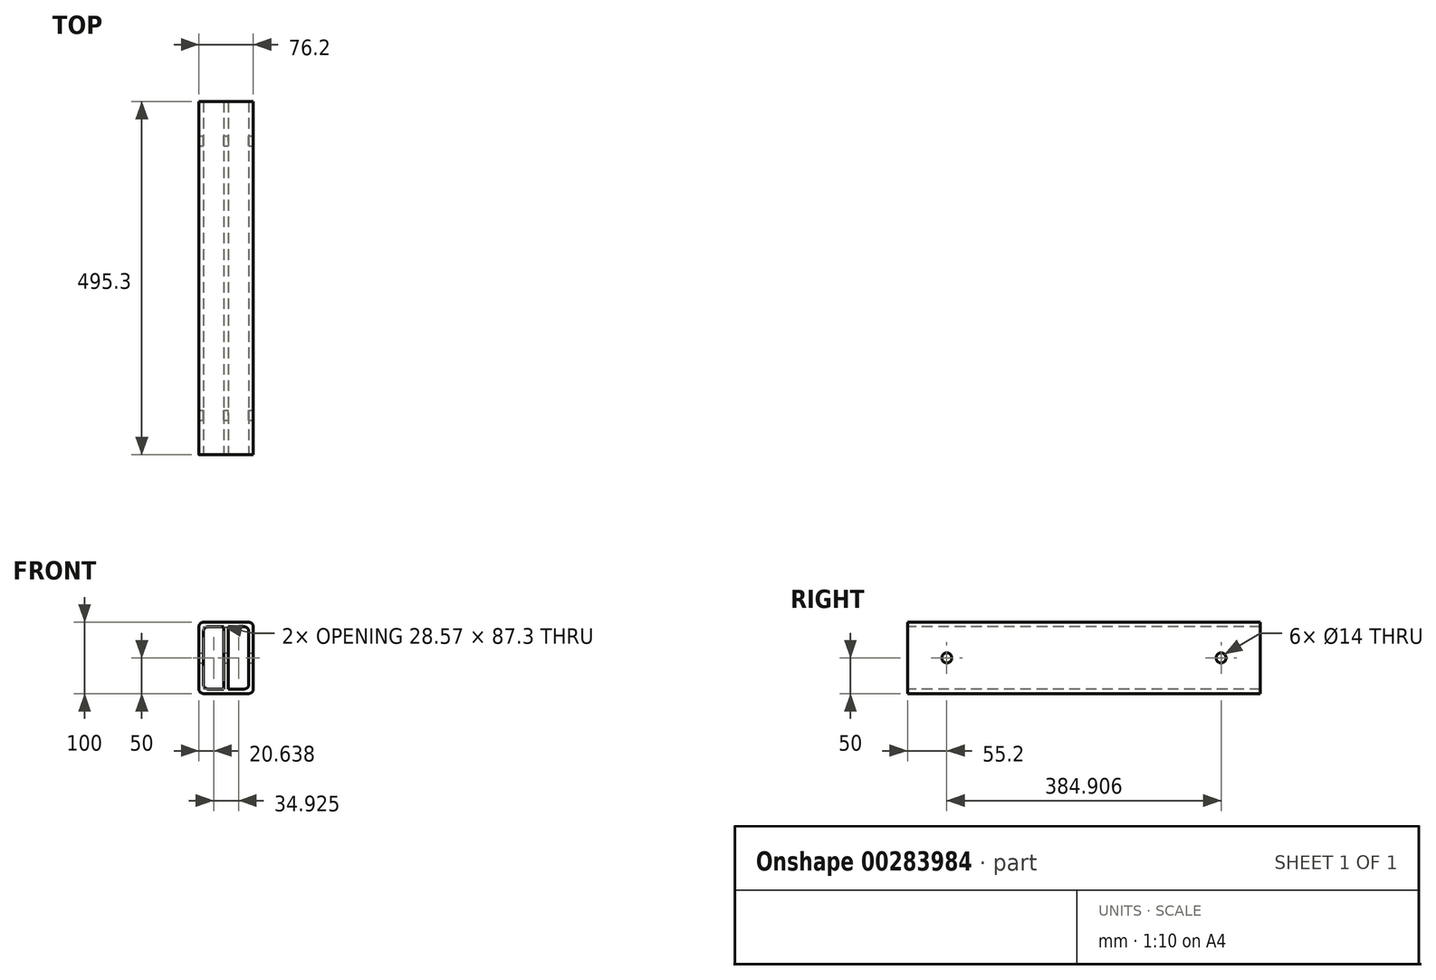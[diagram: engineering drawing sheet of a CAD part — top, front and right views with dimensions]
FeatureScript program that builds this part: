
annotation { "Feature Type Name" : "Feature", "Feature Type Description" : "" }
export const myFeature = defineFeature(function(context is Context, id is Id, definition is map)
    precondition{}
    {
        {
            var Q0;
            Q0=qCreatedBy(makeId("Front.planeOp"),FACE);
            var sketch = newSketch(context, id + "F0", { "sketchPlane" : qUnion([Q0])});
            skLineSegment(sketch, "E0.bottom", {"start": v(31.75, -50) * mm, "end": v(-31.75, -50) * mm});
            skLineSegment(sketch, "E0.top", {"start": v(31.75, 50) * mm, "end": v(-31.75, 50) * mm});
            skLineSegment(sketch, "E0.left", {"start": v(38.1, -43.65) * mm, "end": v(38.1, 43.65) * mm});
            skLineSegment(sketch, "E0.right", {"start": v(-38.1, -43.65) * mm, "end": v(-38.1, 43.65) * mm});
            skPoint(sketch, "E0.middle", {"position": v(0, 0) * mm});
            skLineSegment(sketch, "E1.bottom", {"start": v(25.4, -43.65) * mm, "end": v(-25.4, -43.65) * mm});
            skLineSegment(sketch, "E1.top", {"start": v(25.4, 43.65) * mm, "end": v(-25.4, 43.65) * mm});
            skLineSegment(sketch, "E1.left", {"start": v(31.75, -37.3) * mm, "end": v(31.75, 37.3) * mm});
            skLineSegment(sketch, "E1.right", {"start": v(-31.75, -37.3) * mm, "end": v(-31.75, 37.3) * mm});
            skPoint(sketch, "E2.visualSharp", {"position": v(-38.1, 50) * mm});
            skArc(sketch, "E2.filletArc", {"start": v(-31.75, 50) * mm, "mid": v(-36.24, 48.14) * mm, "end": v(-38.1, 43.65) * mm});
            skArc(sketch, "E3.filletArc", {"start": v(-25.4, 43.65) * mm, "mid": v(-29.9, 41.8) * mm, "end": v(-31.75, 37.3) * mm});
            skPoint(sketch, "E4.visualSharp", {"position": v(31.75, 43.65) * mm});
            skArc(sketch, "E4.filletArc", {"start": v(31.75, 37.3) * mm, "mid": v(29.9, 41.8) * mm, "end": v(25.4, 43.65) * mm});
            skPoint(sketch, "E5.visualSharp", {"position": v(38.1, 50) * mm});
            skArc(sketch, "E5.filletArc", {"start": v(38.1, 43.65) * mm, "mid": v(36.24, 48.14) * mm, "end": v(31.75, 50) * mm});
            skPoint(sketch, "E6.visualSharp", {"position": v(31.75, -43.65) * mm});
            skArc(sketch, "E6.filletArc", {"start": v(25.4, -43.65) * mm, "mid": v(29.9, -41.8) * mm, "end": v(31.75, -37.3) * mm});
            skPoint(sketch, "E7.visualSharp", {"position": v(38.1, -50) * mm});
            skArc(sketch, "E7.filletArc", {"start": v(31.75, -50) * mm, "mid": v(36.24, -48.14) * mm, "end": v(38.1, -43.65) * mm});
            skPoint(sketch, "E8.visualSharp", {"position": v(-31.75, -43.65) * mm});
            skArc(sketch, "E8.filletArc", {"start": v(-31.75, -37.3) * mm, "mid": v(-29.9, -41.8) * mm, "end": v(-25.4, -43.65) * mm});
            skPoint(sketch, "E9.visualSharp", {"position": v(-38.1, -50) * mm});
            skArc(sketch, "E9.filletArc", {"start": v(-38.1, -43.65) * mm, "mid": v(-36.24, -48.14) * mm, "end": v(-31.75, -50) * mm});
            skLineSegment(sketch, "E10", {"start": v(-3.18, -43.65) * mm, "end": v(-3.18, 43.65) * mm});
            skLineSegment(sketch, "E11", {"start": v(3.17, 43.65) * mm, "end": v(3.18, -43.65) * mm});
            skSolve(sketch);
        }
        {
            var Q0;
            Q0=makeQuery(id+"F0.imprint","IMPRINT",FACE,{"disambiguationData":[TD([[makeQuery(id+"F0.imprint","IMPRINT",EDGE,{"derivedFrom":sQuery(id+"F0.wireOp",EDGE,"E1.bottom")}),-1.0]])]});
            extrude(context, id + "F1", {"entities" : qUnion([Q0]), "oppositeDirection" : true, "depth" : 6.35 * mm});
        }
        {
            var Q0;
            Q0=makeQuery(id+"F0.imprint","IMPRINT",FACE,{"disambiguationData":[TD([[makeQuery(id+"F0.imprint","IMPRINT",EDGE,{"derivedFrom":sQuery(id+"F0.wireOp",EDGE,"E0.bottom")}),-1.0]])]});
            extrude(context, id + "F2", {"entities" : qUnion([Q0]), "operationType" : NewBodyOperationType.ADD, "oppositeDirection" : true, "depth" : 495.3 * mm});
        }
        {
            var Q0;
            Q0=qCreatedBy(makeId("Front.planeOp"),FACE);
            var sketch = newSketch(context, id + "F3", { "sketchPlane" : qUnion([Q0])});
            skLineSegment(sketch, "E12.bottom", {"start": v(38.1, -101.6) * mm, "end": v(-38.1, -101.6) * mm});
            skLineSegment(sketch, "E12.top", {"start": v(38.1, 101.6) * mm, "end": v(-38.1, 101.6) * mm});
            skLineSegment(sketch, "E12.left", {"start": v(38.1, -101.6) * mm, "end": v(38.1, 101.6) * mm});
            skLineSegment(sketch, "E12.right", {"start": v(-38.1, -101.6) * mm, "end": v(-38.1, 101.6) * mm});
            skPoint(sketch, "E12.middle", {"position": v(0, 0) * mm});
            skLineSegment(sketch, "E13.bottom", {"start": v(31.75, -95.25) * mm, "end": v(-31.75, -95.25) * mm});
            skLineSegment(sketch, "E13.top", {"start": v(31.75, 95.25) * mm, "end": v(-31.75, 95.25) * mm});
            skLineSegment(sketch, "E13.left", {"start": v(31.75, -95.25) * mm, "end": v(31.75, 95.25) * mm});
            skLineSegment(sketch, "E13.right", {"start": v(-31.75, -95.25) * mm, "end": v(-31.75, 95.25) * mm});
            skSolve(sketch);
        }
        {
            var Q0;
            {var subQ0=sQuery(id+"F0.wireOp",EDGE,"E10");Q0=makeQuery(id+"F0.imprint","IMPRINT",FACE,{"disambiguationData":[TD([[makeQuery(id+"F0.imprint","IMPRINT",EDGE,{"derivedFrom":subQ0}),-1.0]])]});}
            extrude(context, id + "F4", {"entities" : qUnion([Q0]), "operationType" : NewBodyOperationType.ADD, "oppositeDirection" : true, "depth" : 495.3 * mm});
        }
        {
            var Q0;
            Q0=makeQuery(id+"F2.opExtrude","SWEPT_FACE",FACE,{"disambiguationData":[OSD([sQuery(id+"F0.wireOp",EDGE,"E0.left")])]});
            var sketch = newSketch(context, id + "F5", { "sketchPlane" : qUnion([Q0])});
            skCircle(sketch, "E14", {"center": v(55.2, 0) * mm, "radius": 7 * mm});
            skCircle(sketch, "E15", {"center": v(440.1, 0) * mm, "radius": 7 * mm});
            skSolve(sketch);
        }
        {
            var Q0;
            Q0=makeQuery(id+"F5.imprint","IMPRINT",FACE,{"disambiguationData":[TD([[makeQuery(id+"F5.imprint","IMPRINT",EDGE,{"derivedFrom":sQuery(id+"F5.wireOp",EDGE,"E14")}),1.0]])]});
            var Q1;
            Q1=makeQuery(id+"F5.imprint","IMPRINT",FACE,{"disambiguationData":[TD([[makeQuery(id+"F5.imprint","IMPRINT",EDGE,{"derivedFrom":sQuery(id+"F5.wireOp",EDGE,"E15")}),1.0]])]});
            extrude(context, id + "F6", {"entities" : qUnion([Q0, Q1]), "operationType" : NewBodyOperationType.REMOVE, "endBound" : BoundingType.THROUGH_ALL, "oppositeDirection" : true, "depth" : 25.4 * mm});
        }
    });
